# Revit family: CNTLED2236W-2450WWT40K
name_source: partatom
category: Lighting Fixtures
units: mm (PartAtom-declared; Revit-internal decimal feet)

## family parameters
Cut with Voids When Loaded = No
Host = Face
Light Source = Yes
Maintain Annotation Orientation = No
Part Type = Normal
Room Calculation Point = No
Round Connector Dimension = Use Diameter
Shared = No

## types (2) — shared parameters
Color Filter = 16777215
Default Elevation = 1219 mm
Dimming Lamp Color Temperature Shift = <None>
Emit from Line Length = 610 mm
HOUSING MATERIAL = HOUSING MATERIAL
Keynote = Para empotrar y suspender en plafón modular y liso, con
ganchos de seguridad en los cuatro extremos. De fácil
instalación.
Lamp = LED
Manufacturer = BEGHELLI
Model = CNTLED2236WWT40K
Tilt Angle = -90.00°
Type Comments = Cuerpo: de aluminio, con pintura acabado blanco.
Difusor: de policarbonato opalino que proporciona una
curva de distribución de 120°.
Type Image = CENTURY IMAGE.PNG
W = 302 mm
WIDTH = 603 mm  [stored 1.97835 ft]

## per-type parameters (varying)
| type | H | HEIGHT | Photometric Web File | Wattage Comments |
| CNTLED2236WWT40 | 302 mm | 603 mm  [stored 1.97835 ft] | CNTLED2236WWT40K-1.IES | 32W |
| CNTLED2450WWT40 | 600 mm | 1200 mm | CNTLED2450WWT40K-1.IES | 52W |

note: [stored X ft] marks values corroborated as IEEE doubles in the binary element streams (Revit-internal decimal feet)

## geometry (parser evidence)
native form markers: Sweep x5
no freeform markers — native parametric forms only
